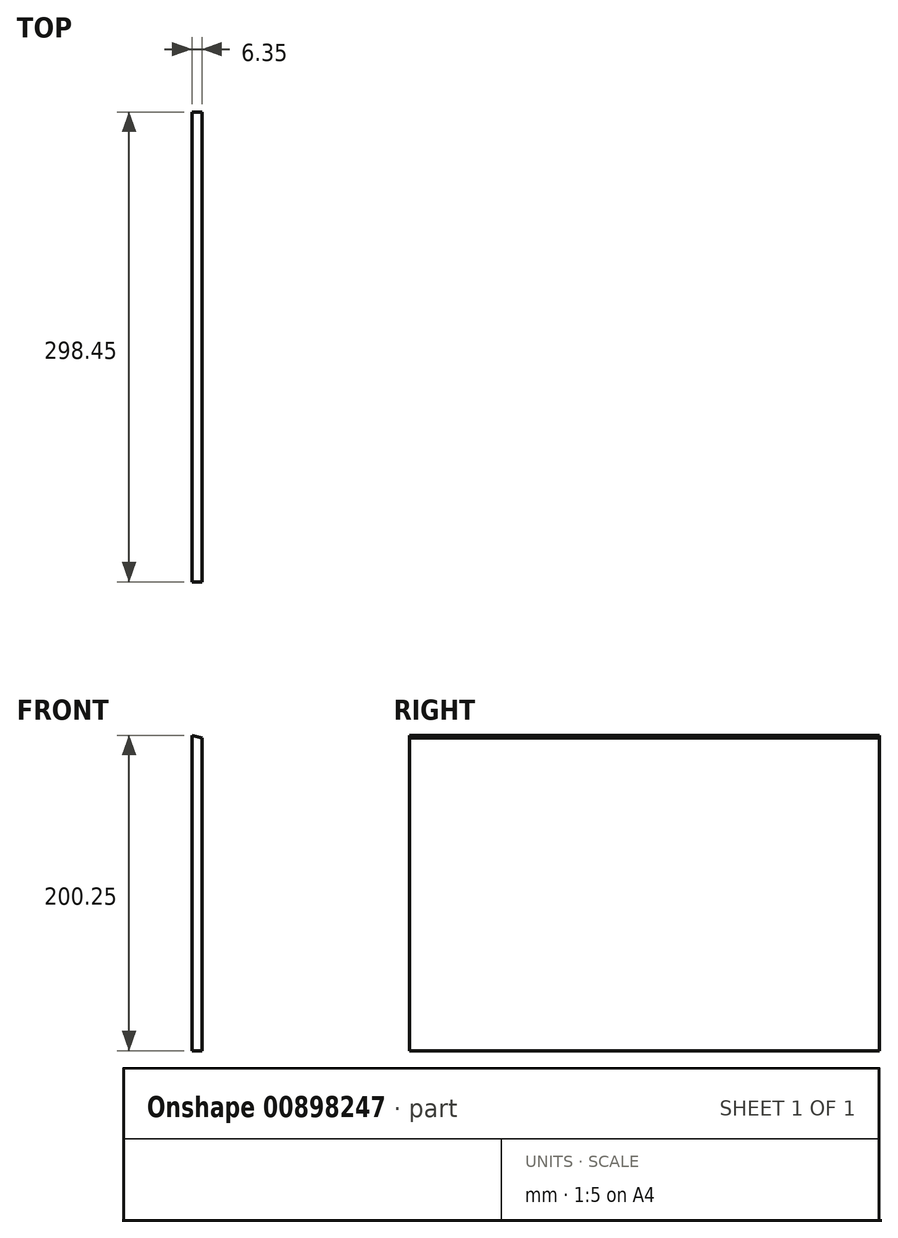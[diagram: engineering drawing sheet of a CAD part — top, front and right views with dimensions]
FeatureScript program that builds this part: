
annotation { "Feature Type Name" : "Feature", "Feature Type Description" : "" }
export const myFeature = defineFeature(function(context is Context, id is Id, definition is map)
    precondition{}
    {
        {
            var Q0;
            Q0=qCreatedBy(makeId("Front.planeOp"),FACE);
            var sketch = newSketch(context, id + "F0", { "sketchPlane" : qUnion([Q0])});
            skLineSegment(sketch, "E0.bottom", {"start": v(0, 0) * mm, "end": v(-6.35, 0) * mm});
            skLineSegment(sketch, "E0.left", {"start": v(0, 0) * mm, "end": v(0, 198.6) * mm});
            skLineSegment(sketch, "E0.right", {"start": v(-6.35, 0) * mm, "end": v(-6.35, 200.25) * mm});
            skLineSegment(sketch, "E1", {"start": v(-6.35, 200.25) * mm, "end": v(0, 198.6) * mm});
            skSolve(sketch);
        }
        {
            var Q0;
            Q0 = qSketchRegion(id + "F0", true);
            extrude(context, id + "F1", {"entities" : qUnion([Q0]), "oppositeDirection" : true, "depth" : 298.45 * mm, "offsetDistance" : 25.4 * mm});
        }
    });
